# Revit family: Gleitschlitten Typ B, höhe h=150mm, Ø219 bis Ø457mm, m.D
name_source: partatom
category: HLS-Bauteile
revit_build: Autodesk Revit 2018 (Build: 20190510_1515(x64)
units: mm (PartAtom-declared; Revit-internal decimal feet)

## family parameters
Arbeitsebenenbasiert = Ja
Beim Laden mit Abzugskörper schneiden = Nein
Bemaßung runder Anschluss = Durchmesser verwenden
Gemeinsam genutzt = Ja
Immer vertikal = Nein
Klassifizierung = Keine
Raumberechnungspunkt = Nein
Teiletyp = Normal

## types (11) — shared parameters
Baustoffklasse = B2
Breite Schellenband = 50 mm
Dämmstärke = 6 mm  [stored 0.019685 ft]
Fabrikat = MEFA
Kurztext1 = Gleitschlitten B 50 x 5 mm
L = 190 mm  [stored 0.62336 ft]
Länge Unterbau = 270 mm
Mengeneinheit = St
Schalldämmeinlage = Gummi EPDM
Sicherheitsfaktor = 1.54
Stärke Schellenband = 5 mm
Verschluss = Schraube + Mutter
Verschluss-Schraube = M12
Vorgabe-Ansicht = 1219 mm
max. Temperaturbeständigkeit = 100 °C
vpe = 1

## per-type parameters (varying)
| type | A (Breite) | Achshöhe | Artikelnummer | Breite Unterbau | EAN | Flachmaterial | Gewicht | Gewicht pro Bauteil | Kurztext2 | RS Titan HD, o.D., Ø219 bis Ø457, 30Grad | Rohraußendurchmesser | Schuh | Stärke Material |
| Gleitschlitten TypB, h=150mm, m.D., Ø219mm | 114 mm  [stored 0.374016 ft] | 260 mm | 110bfb0219 | 253 mm | 4250928462213 | Flachmaterial nach DIN (50-5 und 70-8) : für Ø219 | 10.84 kg | 10.84 kg | 219 mm EPDM fsv | Rohrschelle Titan HD, Gummi,Ø219 30 Grad ok : für Ø219 | 219 mm  [stored 0.718504 ft] | TL-Fuß für Gleitschl.2Lo.14 : 9000852 | 6 mm  [stored 0.019685 ft] |
| Gleitschlitten TypB, h=150mm, m.D., Ø225mm | 114 mm  [stored 0.374016 ft] | 263 mm | 110bfb0225 | 253 mm | 4250928462220 | Flachmaterial nach DIN (50-5 und 70-8) : für Ø225 | 10.94 kg | 10.94 kg | 225 mm EPDM fsv | Rohrschelle Titan HD, Gummi, 30 Grad ok : für Ø225 | 225 mm  [stored 0.738189 ft] | TL-Fuß für Gleitschl.2Lo.14 : 9000852 | 6 mm  [stored 0.019685 ft] |
| Gleitschlitten TypB, h=150mm, m.D., Ø273mm | 128 mm  [stored 0.419948 ft] | 287 mm | 110bfb0273 | 269 mm | 4250928462237 | Flachmaterial nach DIN (50-5 und 70-8) : für Ø273 | 11.79 kg | 11.79 kg | 273 mm EPDM fsv | Rohrschelle Titan HD, Gummi, 30 Grad ok : für Ø273 | 273 mm  [stored 0.895669 ft] | TL-Fuß für Gleitschl.2Lo.14 : 9000852 | 6 mm  [stored 0.019685 ft] |
| Gleitschlitten TypB, h=150mm, m.D., Ø280mm | 128 mm  [stored 0.419948 ft] | 290 mm | 110bfb0280 | 269 mm | 4250928462244 | Flachmaterial nach DIN (50-5 und 70-8) : für Ø280 | 11.90 kg | 11.90 kg | 280 mm EPDM fsv | Rohrschelle Titan HD, Gummi, 30 Grad ok : für Ø280 | 280 mm  [stored 0.918635 ft] | TL-Fuß für Gleitschl.2Lo.14 : 9000852 | 6 mm  [stored 0.019685 ft] |
| Gleitschlitten TypB, h=150mm, m.D., Ø315mm | 138 mm  [stored 0.452756 ft] | 308 mm | 110bfb0315 | 280 mm | 4250928462251 | Flachmaterial nach DIN (50-5 und 70-8) : für Ø315 | 12.51 kg | 12.51 kg | 315 mm EPDM fsv | Rohrschelle Titan HD, Gummi, 30 Grad ok : für Ø315 | 315 mm  [stored 1.03346 ft] | TL-Fuß für Gleitschl.2Lo.14 : 9000852 | 6 mm  [stored 0.019685 ft] |
| Gleitschlitten TypB, h=150mm, m.D., Ø324mm | 138 mm  [stored 0.452756 ft] | 312 mm | 110bfb0324 | 280 mm | 4250928462268 | Flachmaterial nach DIN (50-5 und 70-8) : für Ø324 | 12.66 kg | 12.66 kg | 324 mm EPDM fsv | Rohrschelle Titan HD, Gummi, 30 Grad ok : für Ø324 | 324 mm  [stored 1.06299 ft] | TL-Fuß für Gleitschl.2Lo.14 : 9000852 | 6 mm  [stored 0.019685 ft] |
| Gleitschlitten TypB, h=150mm, m.D., Ø356mm | 146 mm  [stored 0.479003 ft] | 328 mm | 110bfb0356 | 290 mm | 4250928462275 | Flachmaterial nach DIN (50-5 und 70-8) : für Ø356 | 13.20 kg | 13.20 kg | 356 mm EPDM fsv | Rohrschelle Titan HD, Gummi, 30 Grad ok : für Ø356 | 356 mm  [stored 1.16798 ft] | TL-Fuß für Gleitschl.2Lo.14 : 9000852 | 6 mm  [stored 0.019685 ft] |
| Gleitschlitten TypB, h=150mm, m.D., Ø400mm | 177 mm  [stored 0.580709 ft] | 350 mm | 110bfb0400 | 320 mm | 4250928462282 | Flachmaterial nach DIN (50-5 und 70-8) : für Ø400 | 16.98 kg | 16.98 kg | 400 mm EPDM fsv | Rohrschelle Titan HD, Gummi, 30 Grad ok : für Ø400 | 400 mm  [stored 1.31234 ft] | TL-Fuß für Gleitschl.2Lo.14 : 9000853 | 8 mm  [stored 0.0262467 ft] |
| Gleitschlitten TypB, h=150mm, m.D., Ø406mm | 177 mm  [stored 0.580709 ft] | 353 mm | 110bfb0406 | 320 mm | 4250928462299 | Flachmaterial nach DIN (50-5 und 70-8) : für Ø406.4 | 17.10 kg | 17.10 kg | 406 mm EPDM fsv | Rohrschelle Titan HD, Gummi, 30 Grad ok : für Ø406 | 406 mm  [stored 1.33202 ft] | TL-Fuß für Gleitschl.2Lo.14 : 9000853 | 8 mm  [stored 0.0262467 ft] |
| Gleitschlitten TypB, h=150mm, m.D., Ø450mm | 189 mm  [stored 0.620079 ft] | 375 mm | 110bfb0450 | 332 mm | 4250928462305 | Flachmaterial nach DIN (50-5 und 70-8) : für Ø450 | 17.91 kg | 17.91 kg | 450 mm EPDM fsv | Rohrschelle Titan HD, Gummi, 30 Grad ok : für Ø450 | 450 mm  [stored 1.47638 ft] | TL-Fuß für Gleitschl.2Lo.14 : 9000853 | 8 mm  [stored 0.0262467 ft] |
| Gleitschlitten TypB, h=150mm, m.D., Ø457mm | 189 mm  [stored 0.620079 ft] | 379 mm | 110bfb0457 | 332 mm | 4250928462312 | Flachmaterial nach DIN (50-5 und 70-8) : für Ø457 | 18.02 kg | 18.02 kg | 457 mm EPDM fsv | Rohrschelle Titan HD, Gummi, 30 Grad ok : für Ø457 | 457 mm  [stored 1.49934 ft] | TL-Fuß für Gleitschl.2Lo.14 : 9000853 | 8 mm  [stored 0.0262467 ft] |

note: [stored X ft] marks values corroborated as IEEE doubles in the binary element streams (Revit-internal decimal feet)

## geometry (parser evidence)
native form markers: Sweep x9
no freeform markers — native parametric forms only
